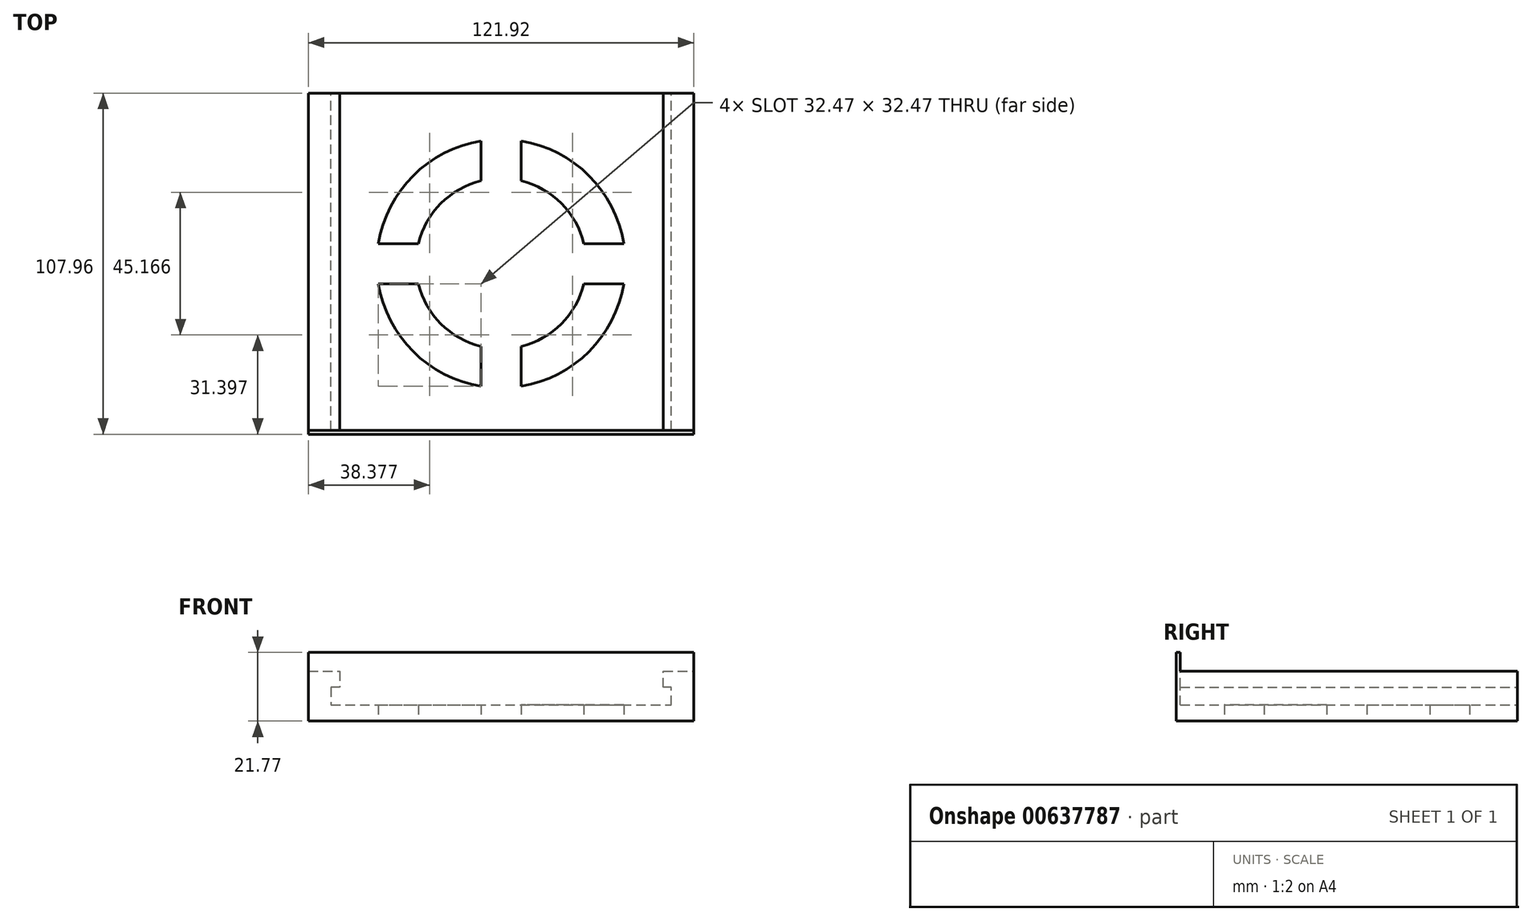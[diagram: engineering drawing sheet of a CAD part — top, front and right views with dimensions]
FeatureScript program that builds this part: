
annotation { "Feature Type Name" : "Feature", "Feature Type Description" : "" }
export const myFeature = defineFeature(function(context is Context, id is Id, definition is map)
    precondition{}
    {
        {
            var Q0;
            Q0=qCreatedBy(makeId("Top.planeOp"),FACE);
            var sketch = newSketch(context, id + "F0", { "sketchPlane" : qUnion([Q0])});
            skLineSegment(sketch, "E0.bottom", {"start": v(-60.96, -53.98) * mm, "end": v(60.96, -53.97) * mm});
            skLineSegment(sketch, "E0.top", {"start": v(-60.96, 53.98) * mm, "end": v(60.96, 53.98) * mm});
            skLineSegment(sketch, "E0.left", {"start": v(-60.96, -53.98) * mm, "end": v(-60.96, 53.97) * mm});
            skLineSegment(sketch, "E0.right", {"start": v(60.96, -53.97) * mm, "end": v(60.96, 53.98) * mm});
            skSolve(sketch);
        }
        {
            var Q0;
            Q0=makeQuery(id+"F0.imprint","IMPRINT",FACE,{"disambiguationData":[TD([[makeQuery(id+"F0.imprint","IMPRINT",EDGE,{"derivedFrom":sQuery(id+"F0.wireOp",EDGE,"E0.bottom")}),1.0]])]});
            extrude(context, id + "F1", {"entities" : qUnion([Q0]), "depth" : 38.1 * mm, "offsetDistance" : 25.4 * mm});
        }
        {
            var Q0;
            Q0=makeQuery(id+"F1.opExtrude","CAP_FACE",FACE,{"disambiguationData":[OSD([sQuery(id+"F0.wireOp",EDGE,"E0.bottom"),sQuery(id+"F0.wireOp",EDGE,"E0.top"),sQuery(id+"F0.wireOp",EDGE,"E0.left"),sQuery(id+"F0.wireOp",EDGE,"E0.right")])],"isStart":false});
            var sketch = newSketch(context, id + "F2", { "sketchPlane" : qUnion([Q0])});
            skLineSegment(sketch, "E1.bottom", {"start": v(-50.93, 50.93) * mm, "end": v(50.93, 50.93) * mm});
            skLineSegment(sketch, "E1.top", {"start": v(-50.93, -50.93) * mm, "end": v(50.93, -50.93) * mm});
            skLineSegment(sketch, "E1.left", {"start": v(-50.93, 50.93) * mm, "end": v(-50.93, -50.93) * mm});
            skLineSegment(sketch, "E1.right", {"start": v(50.93, 50.93) * mm, "end": v(50.93, -50.93) * mm});
            skSolve(sketch);
        }
        {
            var Q0;
            Q0=makeQuery(id+"F2.imprint","IMPRINT",FACE,{"disambiguationData":[TD([[makeQuery(id+"F2.imprint","IMPRINT",EDGE,{"derivedFrom":sQuery(id+"F2.wireOp",EDGE,"E1.bottom")}),-1.0]])]});
            extrude(context, id + "F3", {"entities" : qUnion([Q0]), "operationType" : NewBodyOperationType.REMOVE, "oppositeDirection" : true, "depth" : 30.48 * mm, "offsetDistance" : 25.4 * mm});
        }
        {
            var Q0;
            Q0=makeQuery(id+"F1.opExtrude","CAP_FACE",FACE,{"disambiguationData":[OSD([sQuery(id+"F0.wireOp",EDGE,"E0.bottom"),sQuery(id+"F0.wireOp",EDGE,"E0.top"),sQuery(id+"F0.wireOp",EDGE,"E0.left"),sQuery(id+"F0.wireOp",EDGE,"E0.right")])],"isStart":true});
            var sketch = newSketch(context, id + "F4", { "sketchPlane" : qUnion([Q0])});
            skArc(sketch, "E2", {"start": v(-6.35, 38.82) * mm, "mid": v(-27.81, 27.81) * mm, "end": v(-38.82, 6.35) * mm});
            skArc(sketch, "E3", {"start": v(-6.35, 26.2) * mm, "mid": v(-19.06, 19.06) * mm, "end": v(-26.2, 6.35) * mm});
            skLineSegment(sketch, "E4.bottom", {"start": v(-38.82, 6.35) * mm, "end": v(-26.2, 6.35) * mm});
            skLineSegment(sketch, "E4.top", {"start": v(-38.82, -6.35) * mm, "end": v(-26.2, -6.35) * mm});
            skLineSegment(sketch, "E5.left", {"start": v(-6.35, 38.82) * mm, "end": v(-6.35, 26.2) * mm});
            skLineSegment(sketch, "E5.right", {"start": v(6.35, 38.82) * mm, "end": v(6.35, 26.2) * mm});
            skLineSegment(sketch, "E6.trimOffspring", {"start": v(-6.35, -26.2) * mm, "end": v(-6.35, -38.82) * mm});
            skLineSegment(sketch, "E7.trimOffspring", {"start": v(6.35, -26.2) * mm, "end": v(6.35, -38.82) * mm});
            skLineSegment(sketch, "E8.trimOffspring", {"start": v(26.2, 6.35) * mm, "end": v(38.82, 6.35) * mm});
            skArc(sketch, "E9.trimOffspring", {"start": v(38.82, 6.35) * mm, "mid": v(27.81, 27.81) * mm, "end": v(6.35, 38.82) * mm});
            skArc(sketch, "E10.trimOffspring", {"start": v(26.2, 6.35) * mm, "mid": v(19.06, 19.06) * mm, "end": v(6.35, 26.2) * mm});
            skLineSegment(sketch, "E11.trimOffspring", {"start": v(26.2, -6.35) * mm, "end": v(38.82, -6.35) * mm});
            skArc(sketch, "E12.trimOffspring", {"start": v(6.35, -26.2) * mm, "mid": v(19.06, -19.06) * mm, "end": v(26.2, -6.35) * mm});
            skArc(sketch, "E13.trimOffspring", {"start": v(6.35, -38.82) * mm, "mid": v(27.81, -27.81) * mm, "end": v(38.82, -6.35) * mm});
            skArc(sketch, "E14.trimOffspring", {"start": v(-26.2, -6.35) * mm, "mid": v(-19.06, -19.06) * mm, "end": v(-6.35, -26.2) * mm});
            skArc(sketch, "E15.trimOffspring", {"start": v(-38.82, -6.35) * mm, "mid": v(-27.81, -27.81) * mm, "end": v(-6.35, -38.82) * mm});
            skSolve(sketch);
        }
        {
            var Q0;
            Q0 = qSketchRegion(id + "F4", true);
            var Q1;
            Q1 = qConstructionFilter(qBodyType(qCreatedBy(id + "F4" ,EDGE), BodyType.WIRE), ConstructionObject.NO);
            extrude(context, id + "F5", {"entities" : qUnion([Q0]), "operationType" : NewBodyOperationType.REMOVE, "surfaceEntities" : qUnion([Q1]), "oppositeDirection" : true, "depth" : 25.4 * mm, "offsetDistance" : 25.4 * mm});
        }
        {
            var Q0;
            Q0=makeQuery(id+"F1.opExtrude","SWEPT_FACE",FACE,{"disambiguationData":[OSD([sQuery(id+"F0.wireOp",EDGE,"E0.top")])]});
            var sketch = newSketch(context, id + "F6", { "sketchPlane" : qUnion([Q0])});
            skLineSegment(sketch, "E16", {"start": v(60.96, 38.1) * mm, "end": v(60.96, 15.75) * mm});
            skLineSegment(sketch, "E17", {"start": v(60.96, 15.75) * mm, "end": v(51.05, 15.75) * mm});
            skLineSegment(sketch, "E18", {"start": v(51.05, 15.75) * mm, "end": v(51.05, 10.67) * mm});
            skLineSegment(sketch, "E19", {"start": v(51.05, 10.67) * mm, "end": v(53.85, 10.67) * mm});
            skLineSegment(sketch, "E20", {"start": v(53.85, 10.67) * mm, "end": v(53.85, 5.08) * mm});
            skLineSegment(sketch, "E21", {"start": v(53.85, 5.08) * mm, "end": v(-53.85, 5.08) * mm});
            skLineSegment(sketch, "E22", {"start": v(-53.85, 5.08) * mm, "end": v(-53.85, 10.67) * mm});
            skLineSegment(sketch, "E23", {"start": v(-53.85, 10.67) * mm, "end": v(-51.3, 10.67) * mm});
            skLineSegment(sketch, "E24", {"start": v(-51.3, 10.67) * mm, "end": v(-51.3, 15.75) * mm});
            skLineSegment(sketch, "E25", {"start": v(-51.3, 15.75) * mm, "end": v(-60.96, 15.75) * mm});
            skLineSegment(sketch, "E26", {"start": v(-60.96, 15.75) * mm, "end": v(-60.96, 38.1) * mm});
            skLineSegment(sketch, "E27", {"start": v(-60.96, 38.1) * mm, "end": v(60.96, 38.1) * mm});
            skSolve(sketch);
        }
        {
            var Q0;
            Q0=makeQuery(id+"F6.imprint","IMPRINT",FACE,{"disambiguationData":[TD([[makeQuery(id+"F6.imprint","IMPRINT",EDGE,{"derivedFrom":sQuery(id+"F6.wireOp",EDGE,"E16")}),-1.0]])]});
            extrude(context, id + "F7", {"entities" : qUnion([Q0]), "operationType" : NewBodyOperationType.REMOVE, "oppositeDirection" : true, "depth" : 106.68 * mm, "offsetDistance" : 25.4 * mm});
        }
        {
            var Q0;
            Q0=makeQuery(id+"F7.boolean.opBoolean","COPY",FACE,{"derivedFrom":makeQuery(id+"F7.opExtrude","CAP_FACE",FACE,{"disambiguationData":[OSD([sQuery(id+"F6.wireOp",EDGE,"E16"),sQuery(id+"F6.wireOp",EDGE,"E17"),sQuery(id+"F6.wireOp",EDGE,"E18"),sQuery(id+"F6.wireOp",EDGE,"E19"),sQuery(id+"F6.wireOp",EDGE,"E20"),sQuery(id+"F6.wireOp",EDGE,"E21"),sQuery(id+"F6.wireOp",EDGE,"E22"),sQuery(id+"F6.wireOp",EDGE,"E23"),sQuery(id+"F6.wireOp",EDGE,"E24"),sQuery(id+"F6.wireOp",EDGE,"E25"),sQuery(id+"F6.wireOp",EDGE,"E27"),sQuery(id+"F6.wireOp",EDGE,"E26")])],"isStart":false})});
            var sketch = newSketch(context, id + "F8", { "sketchPlane" : qUnion([Q0])});
            skLineSegment(sketch, "E28.bottom", {"start": v(-60.96, 38.1) * mm, "end": v(60.96, 38.1) * mm});
            skLineSegment(sketch, "E28.top", {"start": v(-60.96, 21.77) * mm, "end": v(60.96, 21.77) * mm});
            skLineSegment(sketch, "E28.left", {"start": v(-60.96, 38.1) * mm, "end": v(-60.96, 21.77) * mm});
            skLineSegment(sketch, "E28.right", {"start": v(60.96, 38.1) * mm, "end": v(60.96, 21.77) * mm});
            skSolve(sketch);
        }
        {
            var Q0;
            Q0=makeQuery(id+"F8.imprint","IMPRINT",FACE,{"disambiguationData":[TD([[makeQuery(id+"F8.imprint","IMPRINT",EDGE,{"derivedFrom":sQuery(id+"F8.wireOp",EDGE,"E28.bottom")}),1.0]])]});
            extrude(context, id + "F9", {"entities" : qUnion([Q0]), "operationType" : NewBodyOperationType.REMOVE, "oppositeDirection" : true, "depth" : 25.4 * mm, "offsetDistance" : 25.4 * mm});
        }
        {
            var Q0;
            Q0 = qSketchRegion(id + "F4", true);
            extrude(context, id + "F10", {"entities" : qUnion([Q0]), "operationType" : NewBodyOperationType.REMOVE, "oppositeDirection" : true, "depth" : 25.4 * mm, "offsetDistance" : 25.4 * mm});
        }
    });
